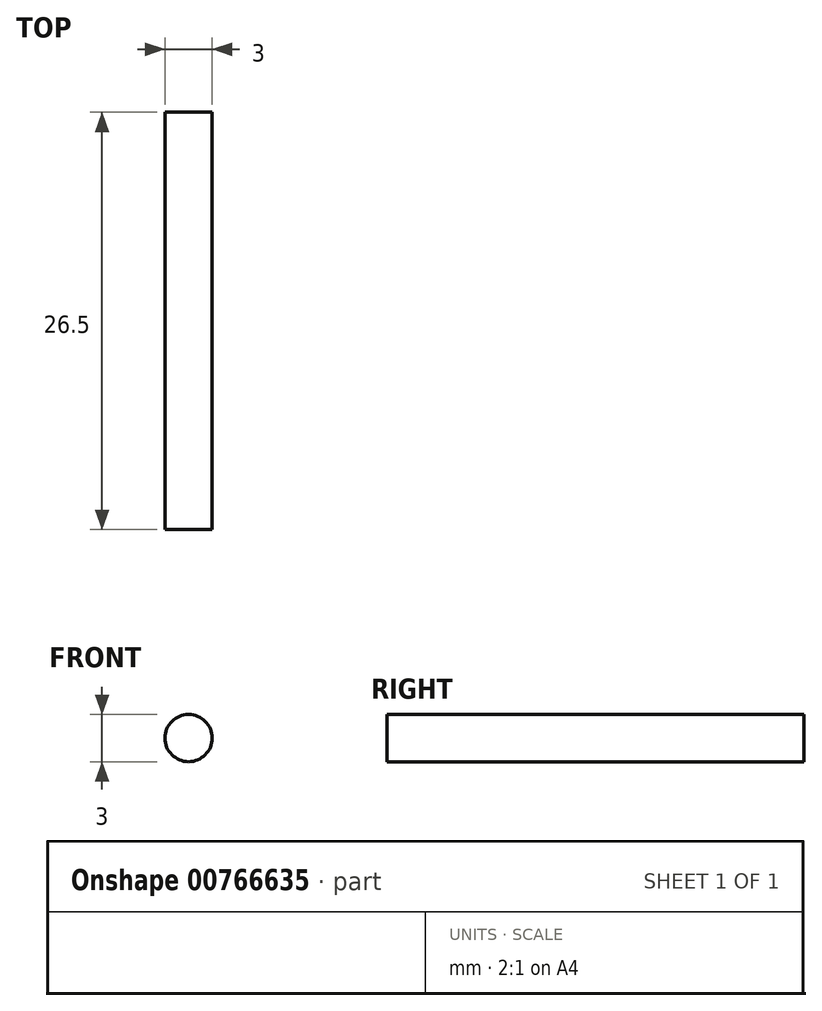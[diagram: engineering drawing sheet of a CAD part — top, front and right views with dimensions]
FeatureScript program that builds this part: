
annotation { "Feature Type Name" : "Feature", "Feature Type Description" : "" }
export const myFeature = defineFeature(function(context is Context, id is Id, definition is map)
    precondition{}
    {
        {
            var Q0;
            Q0=qCreatedBy(makeId("Front.planeOp"),FACE);
            var sketch = newSketch(context, id + "F0", { "sketchPlane" : qUnion([Q0])});
            skCircle(sketch, "E0", {"center": v(0, 0) * mm, "radius": 1.5 * mm});
            skSolve(sketch);
        }
        {
            var Q0;
            Q0 = qSketchRegion(id + "F0", true);
            extrude(context, id + "F1", {"entities" : qUnion([Q0]), "depth" : 26.5 * mm, "offsetDistance" : 25 * mm});
        }
    });
